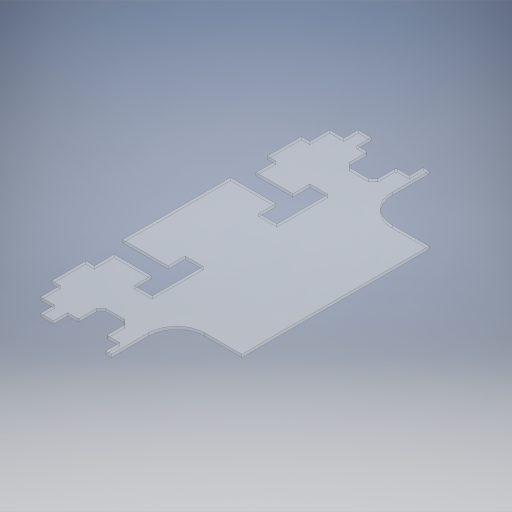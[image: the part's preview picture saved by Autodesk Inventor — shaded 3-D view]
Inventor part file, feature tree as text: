
AUTODESK INVENTOR PART (.ipt)
format: ipt  version: 2024.2 (Build 282272000, 272)  size: 819,712 bytes
history: native  units: in
note: dims shown in document units (in); Inventor stores cm internally (conversion verified against a paired STEP export)
features: extrude x9, sketch x9, projected_geometry x8
ambient origin geometry x8: Origin, YZ Plane, XZ Plane, XY Plane, X Axis, Y Axis, Z Axis, Center Point
bodies: Solid1 (feature_tree)
feature tree (26):
  extrude  "Extrusion1"  Depth=28.0in
  extrude  "Extrusion2"  Depth=3.0in
  extrude  "Extrusion3"  Depth=1.75in
  extrude  "Extrusion4"  Depth=0.25in TaperAngle=0.0deg
  extrude  "Extrusion5"  Depth=1.25in
  extrude  "Extrusion6"  Depth=1.75in
  extrude  "Extrusion7"  Depth=1.25in
  extrude  "Extrusion8"  Depth=5.75in
  extrude  "Extrusion9"  Depth=2.5in
  sketch  "Sketch1"  dims[d0=28.0in d1=28.0in]
  sketch  "Sketch2"  dims[d2=0.25in d3=0.0in d4=3.0in]
  projected_geometry  "Projected Loop1"
  sketch  "Sketch3"  dims[d5=1.25in d6=1.75in]
  projected_geometry  "Projected Loop2"
  sketch  "Sketch4"  dims[d7=1.75in d8=0.25in d9=0.0in]
  projected_geometry  "Projected Loop3"
  sketch  "Sketch5"  dims[d10=6.5in d11=1.25in]
  projected_geometry  "Projected Loop4"
  sketch  "Sketch6"  dims[d12=1.25in d13=1.75in]
  projected_geometry  "Projected Loop5"
  sketch  "Sketch7"  dims[d14=1.5in d15=1.25in]
  projected_geometry  "Projected Loop6"
  sketch  "Sketch8"  dims[d16=0.25in d17=0.0in d18=5.75in]
  projected_geometry  "Projected Loop7"
  sketch  "Sketch9"  dims[d19=5.75in d20=2.5in d21=0.25in d22=0.0in d24=6.25in d25=1.25in d26=1.25in d27=1.05in d30=1.5in d33=1.707in d34=0.846in d35=22.6875in d36=0.0in d38=6.625in d39=14.375in d40=0.0in d42=0.25in d43=0.25in d44=0.5in d45=1.25in d46=1.147in d47=1.25in d48=1.75in d49=1.5in d50=1.75in d51=1.25in d52=0.5in d53=0.5in d54=14.375in d55=0.0in d56=1.5in d57=1.0in d58=0.0in d59=3.125in d60=0.0in]
  projected_geometry  "Projected Loop8"
